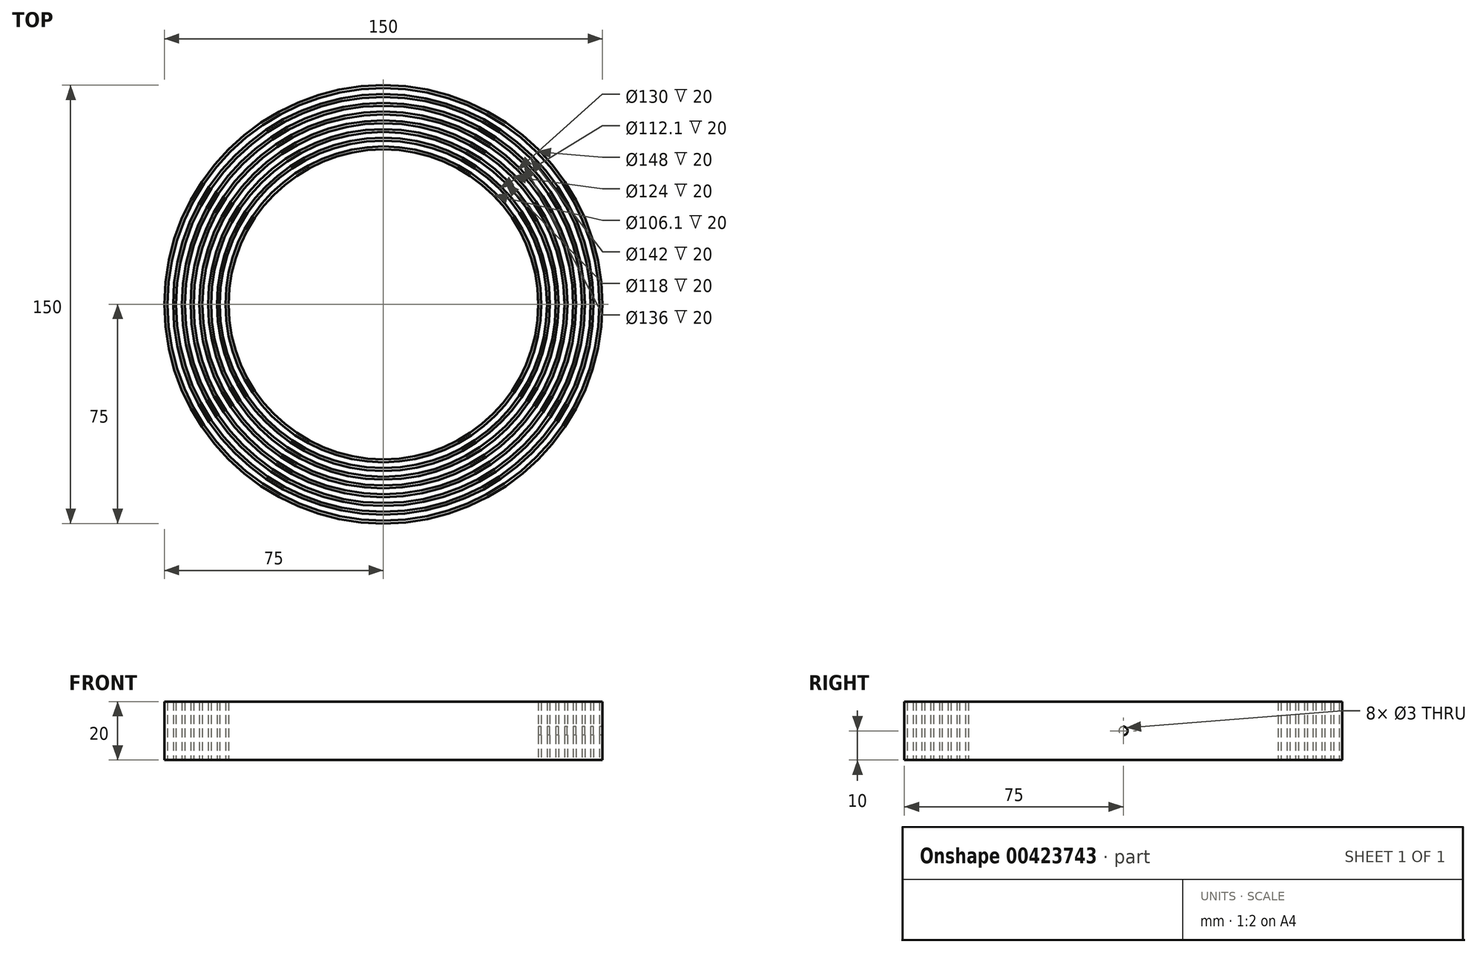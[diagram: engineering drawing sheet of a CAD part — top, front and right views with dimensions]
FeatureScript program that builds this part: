
annotation { "Feature Type Name" : "Feature", "Feature Type Description" : "" }
export const myFeature = defineFeature(function(context is Context, id is Id, definition is map)
    precondition{}
    {
        {
            var Q0;
            Q0=qCreatedBy(makeId("Top.planeOp"),FACE);
            var sketch = newSketch(context, id + "F0", { "sketchPlane" : qUnion([Q0])});
            skCircle(sketch, "E0", {"center": v(0, 0) * mm, "radius": 75 * mm});
            skCircle(sketch, "E1.0", {"center": v(0, 0) * mm, "radius": 74 * mm});
            skCircle(sketch, "E2.0", {"center": v(0, 0) * mm, "radius": 72 * mm});
            skCircle(sketch, "E3.0", {"center": v(0, 0) * mm, "radius": 71 * mm});
            skCircle(sketch, "E4.0", {"center": v(0, 0) * mm, "radius": 69 * mm});
            skCircle(sketch, "E5.0", {"center": v(0, 0) * mm, "radius": 68 * mm});
            skCircle(sketch, "E6.0", {"center": v(0, 0) * mm, "radius": 66 * mm});
            skCircle(sketch, "E7.0", {"center": v(0, 0) * mm, "radius": 65 * mm});
            skCircle(sketch, "E8.0", {"center": v(0, 0) * mm, "radius": 63 * mm});
            skCircle(sketch, "E9.0", {"center": v(0, 0) * mm, "radius": 62 * mm});
            skCircle(sketch, "E10.0", {"center": v(0, 0) * mm, "radius": 60 * mm});
            skCircle(sketch, "E11.0", {"center": v(0, 0) * mm, "radius": 59 * mm});
            skCircle(sketch, "E12.0", {"center": v(0, 0) * mm, "radius": 57 * mm});
            skCircle(sketch, "E13.0", {"center": v(0, 0) * mm, "radius": 56.05 * mm});
            skCircle(sketch, "E14.0", {"center": v(0, 0) * mm, "radius": 54.05 * mm});
            skCircle(sketch, "E15.0", {"center": v(0, 0) * mm, "radius": 53.05 * mm});
            skSolve(sketch);
        }
        {
            var Q0;
            Q0=makeQuery(id+"F0.imprint","IMPRINT",FACE,{"disambiguationData":[TD([[makeQuery(id+"F0.imprint","IMPRINT",EDGE,{"derivedFrom":sQuery(id+"F0.wireOp",EDGE,"E0")}),1.0]])]});
            var Q1;
            Q1=makeQuery(id+"F0.imprint","IMPRINT",FACE,{"disambiguationData":[TD([[makeQuery(id+"F0.imprint","IMPRINT",EDGE,{"derivedFrom":sQuery(id+"F0.wireOp",EDGE,"E2.0")}),1.0]])]});
            var Q2;
            Q2=makeQuery(id+"F0.imprint","IMPRINT",FACE,{"disambiguationData":[TD([[makeQuery(id+"F0.imprint","IMPRINT",EDGE,{"derivedFrom":sQuery(id+"F0.wireOp",EDGE,"E4.0")}),1.0]])]});
            var Q3;
            Q3=makeQuery(id+"F0.imprint","IMPRINT",FACE,{"disambiguationData":[TD([[makeQuery(id+"F0.imprint","IMPRINT",EDGE,{"derivedFrom":sQuery(id+"F0.wireOp",EDGE,"E6.0")}),1.0]])]});
            var Q4;
            Q4=makeQuery(id+"F0.imprint","IMPRINT",FACE,{"disambiguationData":[TD([[makeQuery(id+"F0.imprint","IMPRINT",EDGE,{"derivedFrom":sQuery(id+"F0.wireOp",EDGE,"E8.0")}),1.0]])]});
            var Q5;
            Q5=makeQuery(id+"F0.imprint","IMPRINT",FACE,{"disambiguationData":[TD([[makeQuery(id+"F0.imprint","IMPRINT",EDGE,{"derivedFrom":sQuery(id+"F0.wireOp",EDGE,"E10.0")}),1.0]])]});
            var Q6;
            Q6=makeQuery(id+"F0.imprint","IMPRINT",FACE,{"disambiguationData":[TD([[makeQuery(id+"F0.imprint","IMPRINT",EDGE,{"derivedFrom":sQuery(id+"F0.wireOp",EDGE,"E12.0")}),1.0]])]});
            var Q7;
            Q7=makeQuery(id+"F0.imprint","IMPRINT",FACE,{"disambiguationData":[TD([[makeQuery(id+"F0.imprint","IMPRINT",EDGE,{"derivedFrom":sQuery(id+"F0.wireOp",EDGE,"E14.0")}),1.0]])]});
            var Q8;
            Q8=makeQuery(id+"F0.imprint","IMPRINT",FACE,{"disambiguationData":[TD([[makeQuery(id+"F0.imprint","IMPRINT",EDGE,{"derivedFrom":sQuery(id+"F0.wireOp",EDGE,"8726d99a-e58e-4108-935e-592b3f93d064.0")}),-1.0]])]});
            extrude(context, id + "F1", {"entities" : qUnion([Q0, Q1, Q2, Q3, Q4, Q5, Q6, Q7, Q8]), "depth" : 20 * mm});
        }
        {
            var Q0;
            Q0=qCreatedBy(makeId("Right.planeOp"),FACE);
            var sketch = newSketch(context, id + "F2", { "sketchPlane" : qUnion([Q0])});
            skCircle(sketch, "E16", {"center": v(0, 10) * mm, "radius": 1.5 * mm});
            skSolve(sketch);
        }
        {
            var Q0;
            Q0=qSketchRegion(id+"F2",true);
            extrude(context, id + "F3", {"entities" : qUnion([Q0]), "operationType" : NewBodyOperationType.REMOVE, "depth" : 86.5 * mm});
        }
    });
